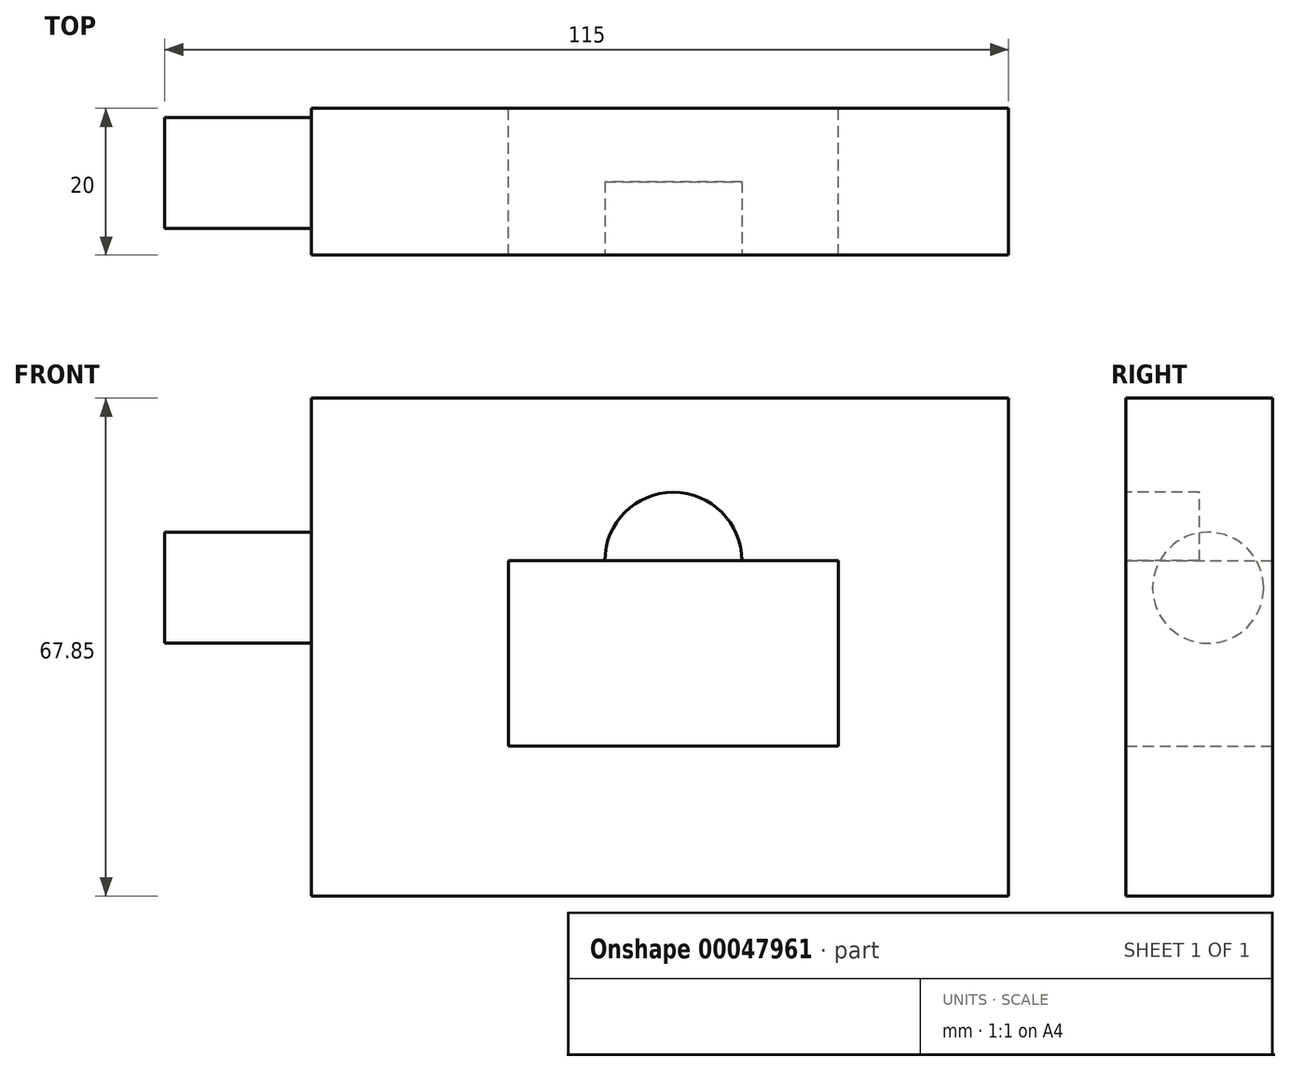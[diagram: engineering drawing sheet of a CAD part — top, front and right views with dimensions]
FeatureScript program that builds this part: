
annotation { "Feature Type Name" : "Feature", "Feature Type Description" : "" }
export const myFeature = defineFeature(function(context is Context, id is Id, definition is map)
    precondition{}
    {
        {
            var Q0;
            Q0=qCreatedBy(makeId("Front.planeOp"),FACE);
            var sketch = newSketch(context, id + "F0", { "sketchPlane" : qUnion([Q0])});
            skLineSegment(sketch, "E0.bottom", {"start": v(-87.28, 34.24) * mm, "end": v(7.72, 34.24) * mm});
            skLineSegment(sketch, "E0.top", {"start": v(-87.28, -33.61) * mm, "end": v(7.72, -33.61) * mm});
            skLineSegment(sketch, "E0.left", {"start": v(-87.28, 34.24) * mm, "end": v(-87.28, -33.61) * mm});
            skLineSegment(sketch, "E0.right", {"start": v(7.72, 34.24) * mm, "end": v(7.72, -33.61) * mm});
            skLineSegment(sketch, "E1.bottom", {"start": v(-60.46, 12.09) * mm, "end": v(-15.47, 12.09) * mm});
            skLineSegment(sketch, "E1.top", {"start": v(-60.46, -13.2) * mm, "end": v(-15.47, -13.2) * mm});
            skLineSegment(sketch, "E1.left", {"start": v(-60.46, 12.09) * mm, "end": v(-60.46, -13.2) * mm});
            skLineSegment(sketch, "E1.right", {"start": v(-15.47, 12.09) * mm, "end": v(-15.47, -13.2) * mm});
            skSolve(sketch);
        }
        {
            var Q0;
            Q0=makeQuery(id+"F0.imprint","IMPRINT",FACE,{"disambiguationData":[TD([[makeQuery(id+"F0.imprint","IMPRINT",EDGE,{"derivedFrom":sQuery(id+"F0.wireOp",EDGE,"E0.bottom")}),-1.0]])]});
            extrude(context, id + "F1", {"entities" : qUnion([Q0]), "depth" : 20 * mm});
        }
        {
            var Q0;
            Q0=makeQuery(id+"F1.opExtrude","SWEPT_FACE",FACE,{"disambiguationData":[OSD([sQuery(id+"F0.wireOp",EDGE,"E0.left")])]});
            var sketch = newSketch(context, id + "F2", { "sketchPlane" : qUnion([Q0])});
            skCircle(sketch, "E2", {"center": v(8.8, 8.4) * mm, "radius": 7.57 * mm});
            skSolve(sketch);
        }
        {
            var Q0;
            Q0=makeQuery(id+"F2.imprint","IMPRINT",FACE,{"disambiguationData":[TD([[makeQuery(id+"F2.imprint","IMPRINT",EDGE,{"derivedFrom":sQuery(id+"F2.wireOp",EDGE,"E2")}),1.0]])]});
            extrude(context, id + "F3", {"entities" : qUnion([Q0]), "operationType" : NewBodyOperationType.ADD, "depth" : 20 * mm});
        }
        {
            var Q0;
            Q0=makeQuery(id+"F1.opExtrude","CAP_FACE",FACE,{"disambiguationData":[OSD([sQuery(id+"F0.wireOp",EDGE,"E0.bottom"),sQuery(id+"F0.wireOp",EDGE,"E0.top"),sQuery(id+"F0.wireOp",EDGE,"E0.left"),sQuery(id+"F0.wireOp",EDGE,"E0.right"),sQuery(id+"F0.wireOp",EDGE,"E1.bottom"),sQuery(id+"F0.wireOp",EDGE,"E1.top"),sQuery(id+"F0.wireOp",EDGE,"E1.left"),sQuery(id+"F0.wireOp",EDGE,"E1.right")])],"isStart":false});
            var sketch = newSketch(context, id + "F4", { "sketchPlane" : qUnion([Q0])});
            skCircle(sketch, "E3", {"center": v(-37.97, 12.09) * mm, "radius": 9.34 * mm});
            skSolve(sketch);
        }
        {
            var Q0;
            {var subQ0=makeQuery(id+"F1.opExtrude","CAP_EDGE",EDGE,{"disambiguationData":[OSD([sQuery(id+"F0.wireOp",EDGE,"E1.bottom")])],"isStart":false});var subQ1=sQuery(id+"F4.wireOp",EDGE,"E3");var subQ3=makeQuery(id+"F4.imprint","INTERSECT",VERTEX,{"disambiguationData":[OD(0.0)],"derivedFrom":[subQ0,subQ1]});Q0=makeQuery(id+"F4.imprint","IMPRINT",FACE,{"disambiguationData":[TD([[makeQuery(id+"F4.imprint","IMPRINT",EDGE,{"disambiguationData":[TD([[subQ3,1.0]])],"derivedFrom":subQ1}),1.0]])]});}
            extrude(context, id + "F5", {"entities" : qUnion([Q0]), "operationType" : NewBodyOperationType.REMOVE, "oppositeDirection" : true, "depth" : 10 * mm});
        }
    });
